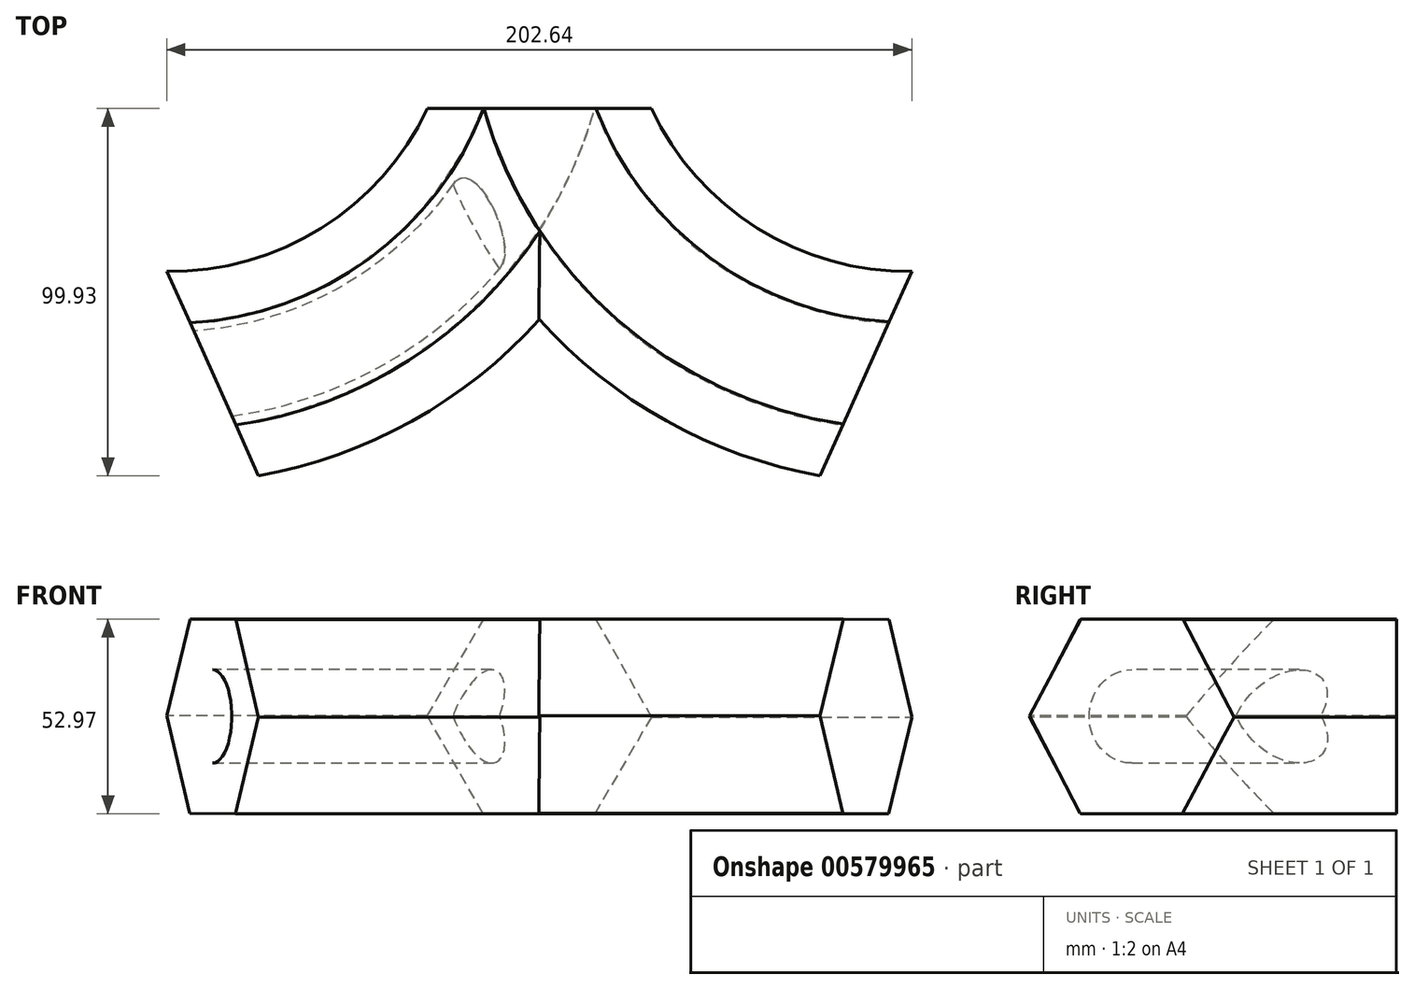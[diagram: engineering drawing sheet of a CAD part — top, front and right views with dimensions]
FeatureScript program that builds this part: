
annotation { "Feature Type Name" : "Feature", "Feature Type Description" : "" }
export const myFeature = defineFeature(function(context is Context, id is Id, definition is map)
    precondition{}
    {
        {
            var Q0;
            Q0=qCreatedBy(makeId("Front.planeOp"),FACE);
            var sketch = newSketch(context, id + "F0", { "sketchPlane" : qUnion([Q0])});
            skCircle(sketch, "E0.cCircle", {"center": v(0, 26.89) * mm, "radius": 26.4 * mm, "construction": true});
            skLineSegment(sketch, "E0.0", {"start": v(-15.4, 0.58) * mm, "end": v(-30.48, 27.07) * mm});
            skLineSegment(sketch, "E0.1", {"start": v(-30.48, 27.07) * mm, "end": v(-15.08, 53.37) * mm});
            skLineSegment(sketch, "E0.2", {"start": v(-15.08, 53.37) * mm, "end": v(15.4, 53.2) * mm});
            skLineSegment(sketch, "E0.3", {"start": v(15.4, 53.2) * mm, "end": v(30.48, 26.7) * mm});
            skLineSegment(sketch, "E0.4", {"start": v(30.48, 26.7) * mm, "end": v(15.08, 0.4) * mm});
            skLineSegment(sketch, "E0.5", {"start": v(15.08, 0.4) * mm, "end": v(-15.4, 0.58) * mm});
            skPoint(sketch, "E0.0.midPoint", {"position": v(-22.94, 13.82) * mm});
            skCircle(sketch, "E1", {"center": v(0, 26.89) * mm, "radius": 12.7 * mm});
            skSolve(sketch);
        }
        {
            var Q0;
            Q0=qCreatedBy(makeId("Top.planeOp"),FACE);
            var sketch = newSketch(context, id + "F1", { "sketchPlane" : qUnion([Q0])});
            skArc(sketch, "E2", {"start": v(-88.86, -72.11) * mm, "mid": v(-33.77, -49.2) * mm, "end": v(0, 0) * mm});
            skArc(sketch, "E3.MirrorCS", {"start": v(88.86, -72.11) * mm, "mid": v(33.77, -49.2) * mm, "end": v(0, 0) * mm});
            skSolve(sketch);
        }
        {
            var Q0;
            Q0=makeQuery(id+"F0.imprint","IMPRINT",FACE,{"disambiguationData":[TD([[makeQuery(id+"F0.imprint","IMPRINT",EDGE,{"derivedFrom":sQuery(id+"F0.wireOp",EDGE,"E0.0")}),-1.0]])]});
            var Q1;
            Q1=sQuery(id+"F1.wireOp",EDGE,"E2");
            sweep(context, id + "F2", {"profiles" : qUnion([Q0]), "path" : qUnion([Q1])});
        }
        {
            var Q0;
            Q0=makeQuery(id+"F0.imprint","IMPRINT",FACE,{"disambiguationData":[TD([[makeQuery(id+"F0.imprint","IMPRINT",EDGE,{"derivedFrom":sQuery(id+"F0.wireOp",EDGE,"E0.0")}),-1.0]])]});
            var Q1;
            Q1=makeQuery(id+"F0.imprint","IMPRINT",FACE,{"disambiguationData":[TD([[makeQuery(id+"F0.imprint","IMPRINT",EDGE,{"derivedFrom":sQuery(id+"F0.wireOp",EDGE,"E1")}),1.0]])]});
            var Q2;
            Q2=sQuery(id+"F1.wireOp",EDGE,"E3.MirrorCS");
            sweep(context, id + "F3", {"operationType" : NewBodyOperationType.ADD, "profiles" : qUnion([Q0, Q1]), "path" : qUnion([Q2])});
        }
    });
